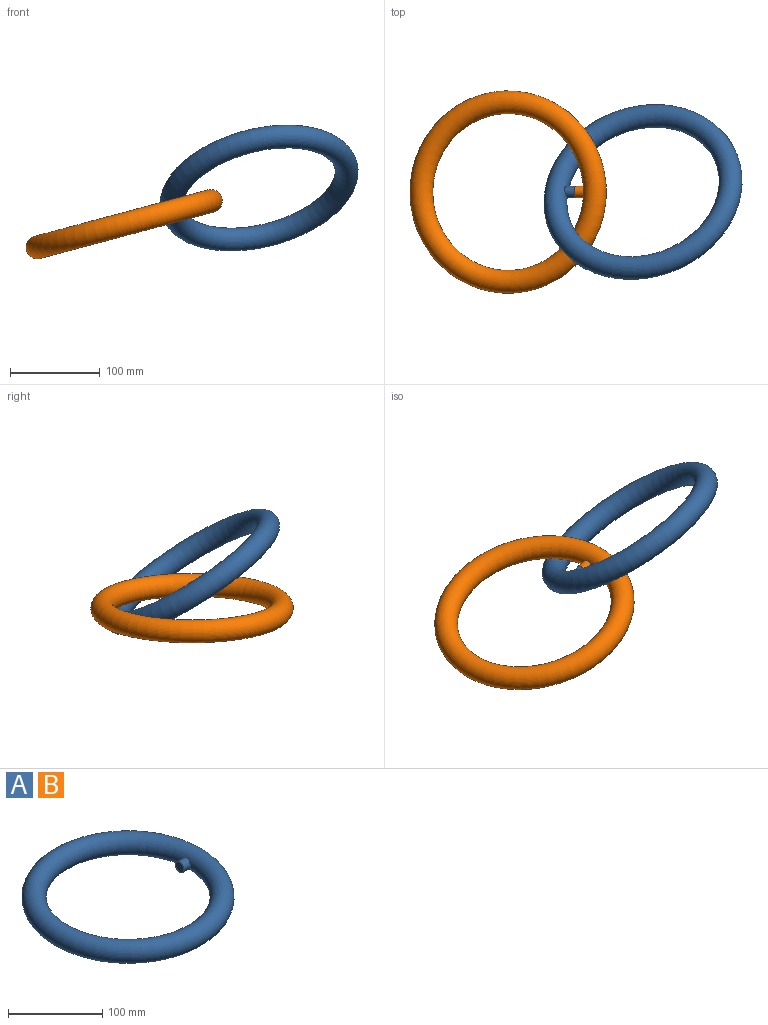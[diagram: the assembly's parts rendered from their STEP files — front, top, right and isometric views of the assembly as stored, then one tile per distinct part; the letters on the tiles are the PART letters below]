
ASSEMBLY  parts=2 mates=1
PART A: 3 faces, bbox 244x244x12.7 mm
  f0: cylinder r=6.35mm len=12.7mm, axis (-1,0,0), area 408.7mm2, adj f1,f2
  f1: plane 12.7x12.7mm, normal (-1,0,0), area 126.7mm2, adj f0
  f2: torus R=100mm, axis (0,0,-1), area 50005.5mm2, adj f0
PART B: same geometry as A
PLACE A rot(axis=(0.04,0.96,-0.28),165.6deg) t=(18.56,46.24,-13.37)mm
PLACE B rot(axis=(0,-1,0),15deg) t=(-131.69,46.24,-53.63)mm
MATE revolute A.f0 <-> B.f0  axis (0.97,0,0.26) through (-56.56,46.24,-33.5)mm
